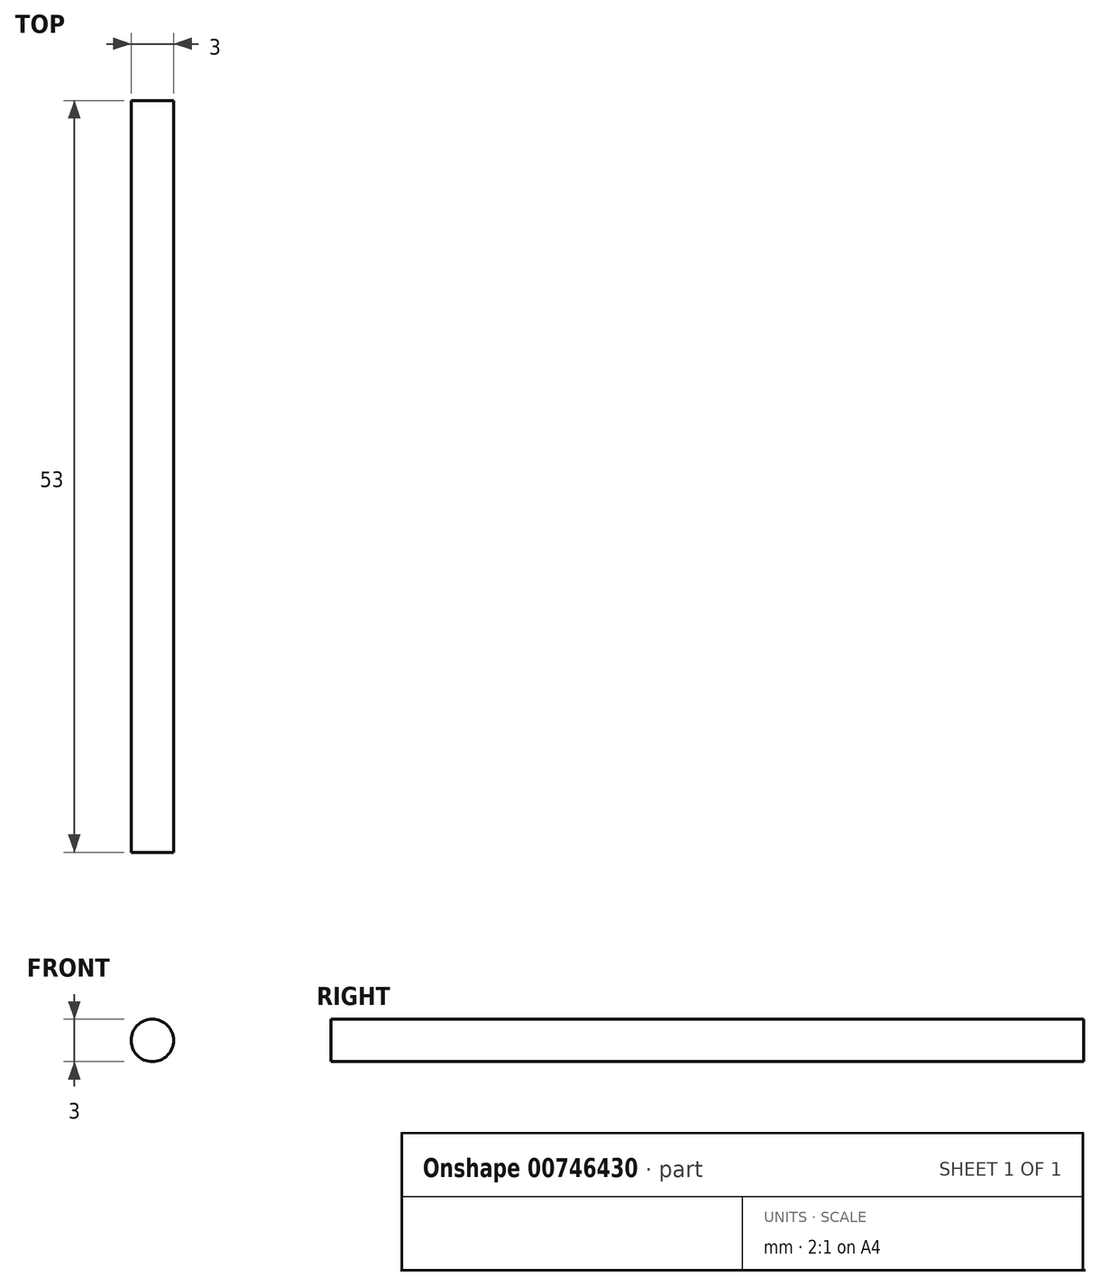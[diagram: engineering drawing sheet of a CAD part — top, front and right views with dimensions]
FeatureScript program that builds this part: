
annotation { "Feature Type Name" : "Feature", "Feature Type Description" : "" }
export const myFeature = defineFeature(function(context is Context, id is Id, definition is map)
    precondition{}
    {
        {
            var Q0;
            Q0=qCreatedBy(makeId("Top.planeOp"),FACE);
            var sketch = newSketch(context, id + "F0", { "sketchPlane" : qUnion([Q0])});
            skCircle(sketch, "E0", {"center": v(0, 0) * mm, "radius": 1.5 * mm});
            skSolve(sketch);
        }
        {
            var Q0;
            Q0 = qSketchRegion(id + "F0", true);
            extrude(context, id + "F1", {"entities" : qUnion([Q0]), "depth" : 53 * mm, "offsetDistance" : 25.4 * mm});
        }
        {
            var Q0;
            Q0=qCreatedBy(makeId("Top.planeOp"),FACE);
            var sketch = newSketch(context, id + "F2", { "sketchPlane" : qUnion([Q0])});
            skLineSegment(sketch, "E1", {"start": v(-22.05, 0) * mm, "end": v(29.7, 0) * mm});
            skSolve(sketch);
        }
        {
            var Q0;
            Q0=makeQuery(id+"F1.opExtrude","SWEPT_BODY",BODY,{"disambiguationData":[OSD([sQuery(id+"F0.wireOp",EDGE,"E0")])]});
            var Q1;
            Q1=sQuery(id+"F2.wireOp",EDGE,"E1");
            transform(context, id + "F3", {"entities" : qUnion([Q0]), "transformType" : TransformType.ROTATION, "transformAxis" : qUnion([Q1]), "angle" : 90 * degree, "makeCopy" : false});
        }
    });
